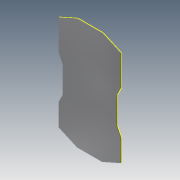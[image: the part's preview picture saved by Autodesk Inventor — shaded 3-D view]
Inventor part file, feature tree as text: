
AUTODESK INVENTOR PART (.ipt)
format: ipt  version: 2013 (Build 170138000, 138)  size: 141,824 bytes
history: native  units: mm
features: sketch x7, extrude x1
ambient origin geometry x8: Origin, YZ Plane, XZ Plane, XY Plane, X Axis, Y Axis, Z Axis, Center Point
bodies: Solid1 (feature_tree)
feature tree (8):
  extrude  "Extrusion1"  [1 undecoded]
  sketch  "Sketch2"
  sketch  "Sketch3"
  sketch  "Sketch4"
  sketch  "Sketch5"
  sketch  "Sketch6"
  sketch  "Sketch7"
  sketch  "Sketch1"  dims[d24=2.0mm d25=0.0mm]
note: 1 required parameter value undecoded (feature->parameter linkage not recoverable at this tier; creation-order binding heuristic only, values carry confidence <= 0.55)
